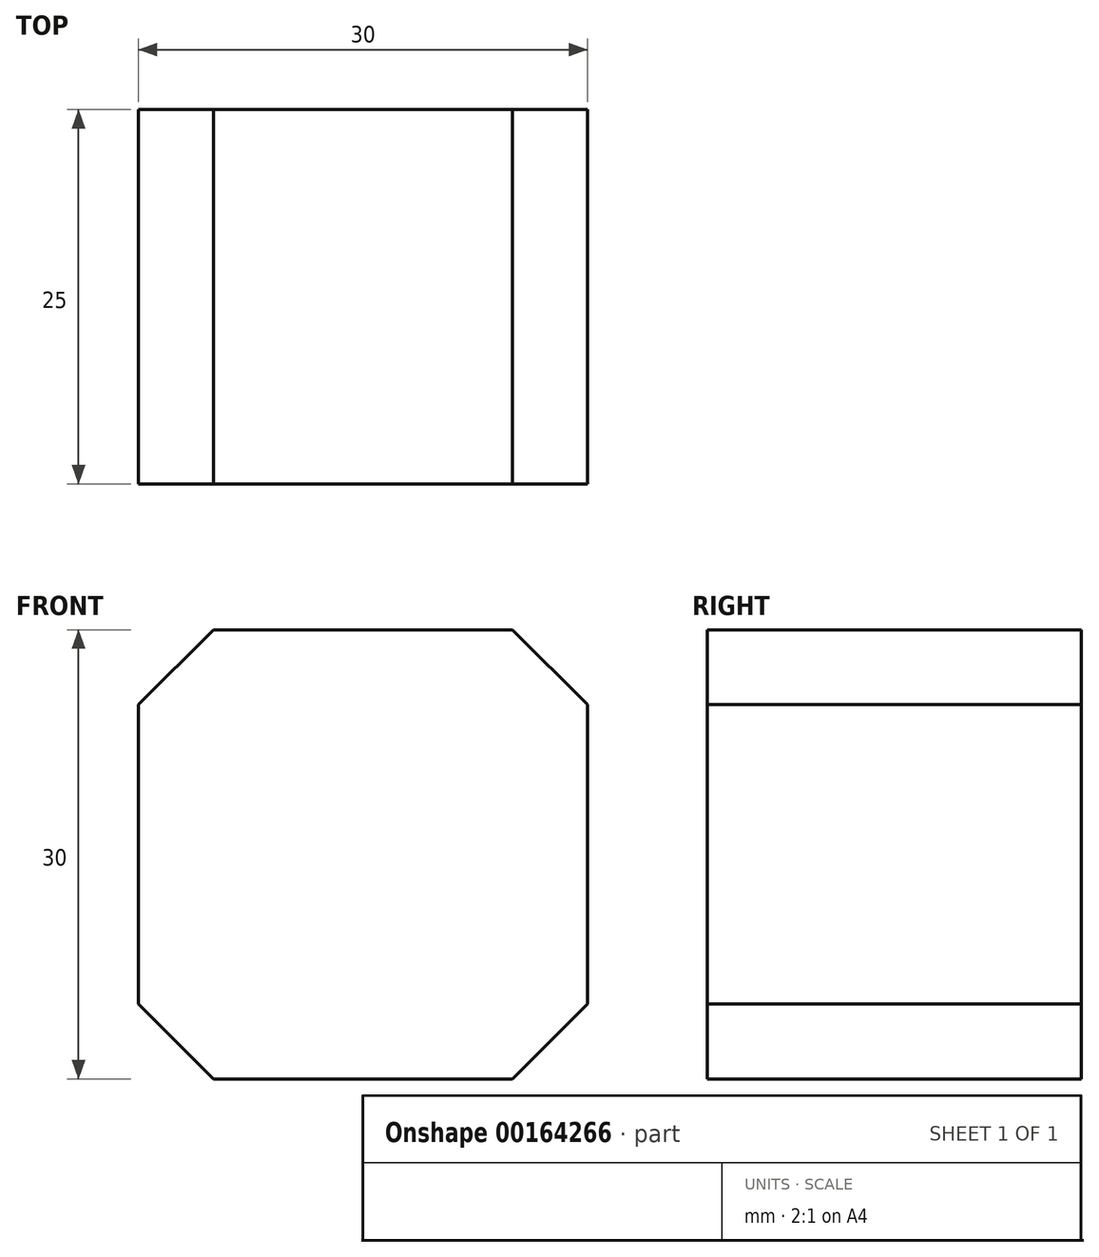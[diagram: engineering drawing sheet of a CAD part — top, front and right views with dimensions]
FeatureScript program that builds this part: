
annotation { "Feature Type Name" : "Feature", "Feature Type Description" : "" }
export const myFeature = defineFeature(function(context is Context, id is Id, definition is map)
    precondition{}
    {
        {
            var Q0;
            Q0=qCreatedBy(makeId("Front.planeOp"),FACE);
            var sketch = newSketch(context, id + "F0", { "sketchPlane" : qUnion([Q0])});
            skLineSegment(sketch, "E0.bottom", {"start": v(-17.5, 12.5) * mm, "end": v(12.5, 12.5) * mm});
            skLineSegment(sketch, "E0.top", {"start": v(-17.5, -17.5) * mm, "end": v(12.5, -17.5) * mm});
            skLineSegment(sketch, "E0.left", {"start": v(-17.5, 12.5) * mm, "end": v(-17.5, -17.5) * mm});
            skLineSegment(sketch, "E0.right", {"start": v(12.5, 12.5) * mm, "end": v(12.5, -17.5) * mm});
            skSolve(sketch);
        }
        {
            var Q0;
            Q0 = qSketchRegion(id + "F0", true);
            extrude(context, id + "F1", {"entities" : qUnion([Q0]), "depth" : 25 * mm});
        }
        {
            var Q0;
            Q0=makeQuery(id+"F1.opExtrude","SWEPT_EDGE",EDGE,{"disambiguationData":[OSD([sQuery(id+"F0.wireOp",EDGE,"E0.bottom"),sQuery(id+"F0.wireOp",EDGE,"E0.left")])]});
            var Q1;
            Q1=makeQuery(id+"F1.opExtrude","SWEPT_EDGE",EDGE,{"disambiguationData":[OSD([sQuery(id+"F0.wireOp",EDGE,"E0.bottom"),sQuery(id+"F0.wireOp",EDGE,"E0.right")])]});
            var Q2;
            Q2=makeQuery(id+"F1.opExtrude","SWEPT_EDGE",EDGE,{"disambiguationData":[OSD([sQuery(id+"F0.wireOp",EDGE,"E0.top"),sQuery(id+"F0.wireOp",EDGE,"E0.left")])]});
            var Q3;
            Q3=makeQuery(id+"F1.opExtrude","SWEPT_EDGE",EDGE,{"disambiguationData":[OSD([sQuery(id+"F0.wireOp",EDGE,"E0.top"),sQuery(id+"F0.wireOp",EDGE,"E0.right")])]});
            chamfer(context, id + "F2", {"entities" : qUnion([Q0, Q1, Q2, Q3]), "width" : 5 * mm, "tangentPropagation" : true});
        }
    });
